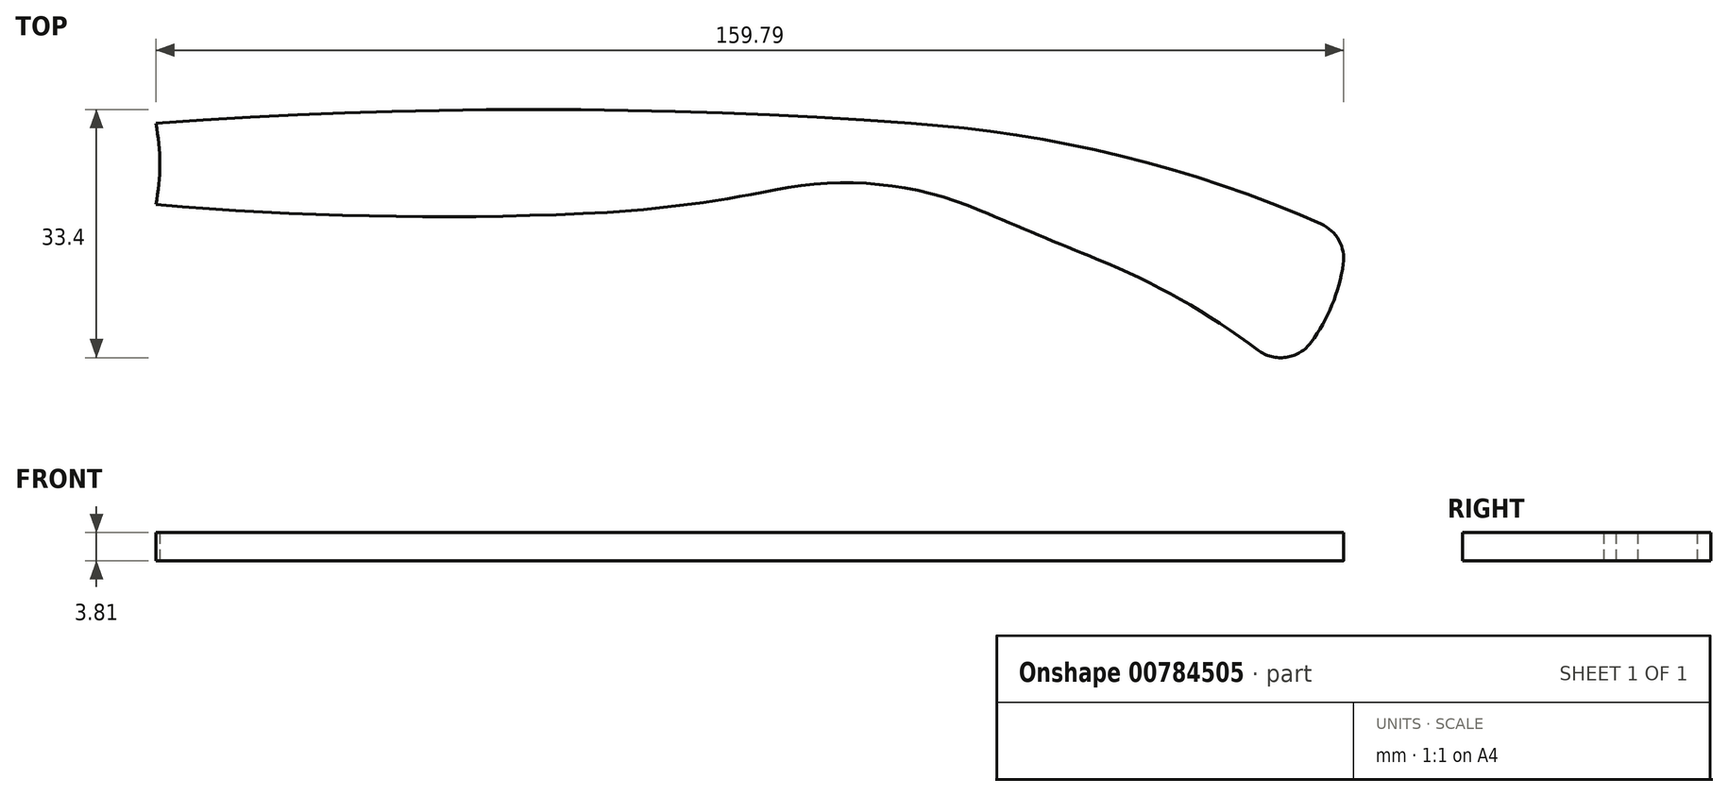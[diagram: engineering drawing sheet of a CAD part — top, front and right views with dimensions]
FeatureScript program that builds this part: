
annotation { "Feature Type Name" : "Feature", "Feature Type Description" : "" }
export const myFeature = defineFeature(function(context is Context, id is Id, definition is map)
    precondition{}
    {
        {
            var Q0;
            Q0=qCreatedBy(makeId("Top.planeOp"),FACE);
            var sketch = newSketch(context, id + "F0", { "sketchPlane" : qUnion([Q0])});
            skArc(sketch, "E0", {"start": v(101.6, 0) * mm, "mid": v(50.8, 1.88) * mm, "end": v(0, 0) * mm});
            skArc(sketch, "E1", {"start": v(159.98, -14.98) * mm, "mid": v(131.49, -4.78) * mm, "end": v(101.6, 0) * mm});
            skArc(sketch, "E2", {"start": v(151.83, -33.32) * mm, "mid": v(157.95, -25.06) * mm, "end": v(159.98, -14.98) * mm});
            skArc(sketch, "E3", {"start": v(151.83, -33.32) * mm, "mid": v(135.46, -22.36) * mm, "end": v(117.19, -14.98) * mm});
            skArc(sketch, "E4", {"start": v(117.19, -14.98) * mm, "mid": v(97.29, -8.2) * mm, "end": v(76.43, -10.9) * mm});
            skArc(sketch, "E5", {"start": v(0, -10.9) * mm, "mid": v(38.22, -12.54) * mm, "end": v(76.43, -10.9) * mm});
            skArc(sketch, "E6", {"start": v(0, -10.9) * mm, "mid": v(0.53, -5.45) * mm, "end": v(0, 0) * mm});
            skSolve(sketch);
        }
        {
            var Q0;
            Q0=makeQuery(id+"F0.imprint","IMPRINT",FACE,{"disambiguationData":[TD([[makeQuery(id+"F0.imprint","IMPRINT",EDGE,{"derivedFrom":sQuery(id+"F0.wireOp",EDGE,"E0")}),1.0]])]});
            extrude(context, id + "F1", {"entities" : qUnion([Q0]), "depth" : 3.8 * mm, "offsetDistance" : 25.4 * mm});
        }
        {
            var Q0;
            Q0=makeQuery(id+"F1.opExtrude","SWEPT_EDGE",EDGE,{"disambiguationData":[OSD([sQuery(id+"F0.wireOp",EDGE,"E2"),sQuery(id+"F0.wireOp",EDGE,"E3")])]});
            var Q1;
            Q1=makeQuery(id+"F1.opExtrude","SWEPT_EDGE",EDGE,{"disambiguationData":[OSD([sQuery(id+"F0.wireOp",EDGE,"E1"),sQuery(id+"F0.wireOp",EDGE,"E2")])]});
            fillet(context, id + "F2", {"entities" : qUnion([Q0, Q1]), "radius" : 5.08 * mm, "tangentPropagation" : true, "allowEdgeOverflow" : false});
        }
        {
            var Q0;
            Q0=makeQuery(id+"F1.opExtrude","SWEPT_EDGE",EDGE,{"disambiguationData":[OSD([sQuery(id+"F0.wireOp",EDGE,"E3"),sQuery(id+"F0.wireOp",EDGE,"E4")])]});
            fillet(context, id + "F3", {"entities" : qUnion([Q0]), "radius" : 865.12 * mm, "tangentPropagation" : true, "allowEdgeOverflow" : false});
        }
        {
            var Q0;
            Q0=makeQuery(id+"F1.opExtrude","SWEPT_EDGE",EDGE,{"disambiguationData":[OSD([sQuery(id+"F0.wireOp",EDGE,"E4"),sQuery(id+"F0.wireOp",EDGE,"E5")])]});
            fillet(context, id + "F4", {"entities" : qUnion([Q0]), "radius" : 162.2 * mm, "tangentPropagation" : true, "allowEdgeOverflow" : false});
        }
    });
